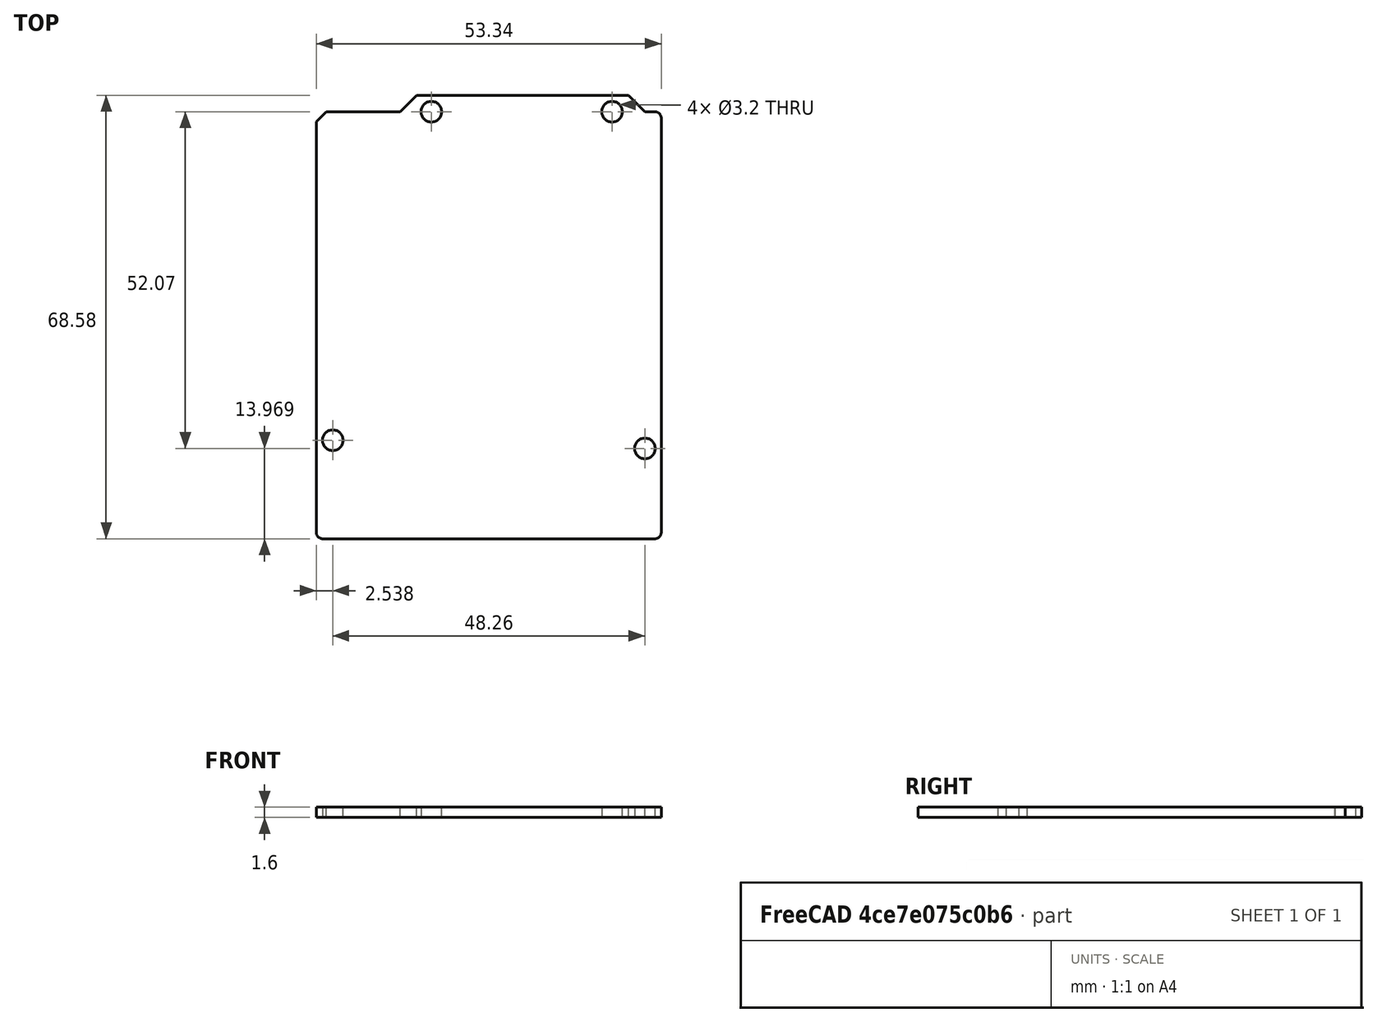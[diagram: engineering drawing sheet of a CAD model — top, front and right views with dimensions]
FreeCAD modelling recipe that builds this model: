
FCSTD DOCUMENT  (FreeCAD 0.14R3703 (Git))
Label: arduino_uno
License: CC-BY 3.0
LicenseURL: http://creativecommons.org/licenses/by/3.0/
objects: Sketcher::SketchObject×1, PartDesign::Pad×1
note: 3 computed .brp shape members not serialized (recipe doc carries the construction recipe); baked Part::Feature solids carry a one-line shape summary decoded from their .brp

FEATURE [Sketcher::SketchObject] Sketch
  sketch-geometry (16):
    g0: LineSegment StartX=-10.8783 StartY=42.0485 StartZ=0 EndX=21.8877 EndY=42.0485 EndZ=0
    g1: LineSegment StartX=21.8877 StartY=42.0485 StartZ=0 EndX=24.4277 EndY=39.5085 EndZ=0
    g2: LineSegment StartX=24.4277 StartY=39.5085 StartZ=0 EndX=25.9677 EndY=39.5085 EndZ=0
    g3: LineSegment StartX=26.9677 StartY=38.5085 StartZ=0 EndX=26.9677 EndY=-25.5315 EndZ=0
    g4: LineSegment StartX=25.9677 StartY=-26.5315 StartZ=0 EndX=-25.3723 EndY=-26.5315 EndZ=0
    g5: LineSegment StartX=-26.3723 StartY=-25.5315 StartZ=0 EndX=-26.3723 EndY=37.9845 EndZ=0
    g6: LineSegment StartX=-26.3723 StartY=37.9845 StartZ=0 EndX=-24.8483 EndY=39.5085 EndZ=0
    g7: LineSegment StartX=-24.8483 StartY=39.5085 StartZ=0 EndX=-13.4183 EndY=39.5085 EndZ=0
    g8: LineSegment StartX=-13.4183 StartY=39.5085 StartZ=0 EndX=-10.8783 EndY=42.0485 EndZ=0
    g9: Circle CenterX=24.4277 CenterY=-12.5615 CenterZ=0 NormalX=0 NormalY=0 NormalZ=1 Radius=1.6
    g10: ArcOfCircle CenterX=25.9677 CenterY=-25.5315 CenterZ=0 NormalX=0 NormalY=0 NormalZ=1 Radius=1 StartAngle=4.71239 EndAngle=6.28319
    g11: ArcOfCircle CenterX=-25.3723 CenterY=-25.5315 CenterZ=0 NormalX=0 NormalY=0 NormalZ=1 Radius=1 StartAngle=3.14159 EndAngle=4.71239
    g12: ArcOfCircle CenterX=25.9677 CenterY=38.5085 CenterZ=0 NormalX=0 NormalY=0 NormalZ=1 Radius=1 StartAngle=0 EndAngle=1.5708
    g13: Circle CenterX=-23.8323 CenterY=-11.2915 CenterZ=0 NormalX=0 NormalY=0 NormalZ=1 Radius=1.6
    g14: Circle CenterX=-8.59234 CenterY=39.5085 CenterZ=0 NormalX=0 NormalY=0 NormalZ=1 Radius=1.6
    g15: Circle CenterX=19.3477 CenterY=39.5085 CenterZ=0 NormalX=0 NormalY=0 NormalZ=1 Radius=1.6
  constraints (43):
    c: Horizontal(g0)
    c: Coincident(g0,g1)
    c: Coincident(g1,g2)
    c: Vertical(g3)
    c: Horizontal(g4)
    c: Vertical(g5)
    c: Coincident(g5,g6)
    c: Coincident(g6,g7)
    c: Horizontal(g7)
    c: Coincident(g7,g8)
    c: Coincident(g8,g0)
    c: Distance(g6,g5) = 1.524
    c: Distance(g7) = 11.43
    c: Horizontal(g2)
    c: Distance(g6,g4) = 66.04
    c: Distance(g5,g7) = 1.524
    c: DistanceX(g8) = 2.54
    c: DistanceX(g0,g1) = 2.54
    c: Radius(g9) = 1.6
    c: Distance(g0,g4) = 68.58
    c: Tangent(g4,g10)
    c: Tangent(g3,g10)
    c: Radius(g10) = 1
    c: Tangent(g5,g11)
    c: Tangent(g4,g11)
    c: Tangent(g2,g12)
    c: Tangent(g3,g12)
    c: Distance(g3,g5) = 53.34
    c: Distance(g1,g0) = 2.54
    c: Distance(g0,g3) = 5.08
    c: Radius(g11) = 1
    c: Radius(g12) = 1
    c: Distance(g9,g4) = 13.97
    c: Distance(g9,g3) = 2.54
    c: Distance(g13,g4) = 15.24
    c: Distance(g13,g5) = 2.54
    c: Radius(g13) = 1.6
    c: DistanceY(g14,g13) = -50.8
    c: Radius(g14) = 1.6
    c: DistanceX(g13,g14) = 15.24
    c: DistanceX(g15,g14) = -27.94
    c: Radius(g15) = 1.6
    c: DistanceY(g15,g13) = -50.8
FEATURE [PartDesign::Pad] Pad
  Length = 1.6
  Length2 = 100
  Sketch = -> Sketch
  Type = 0
